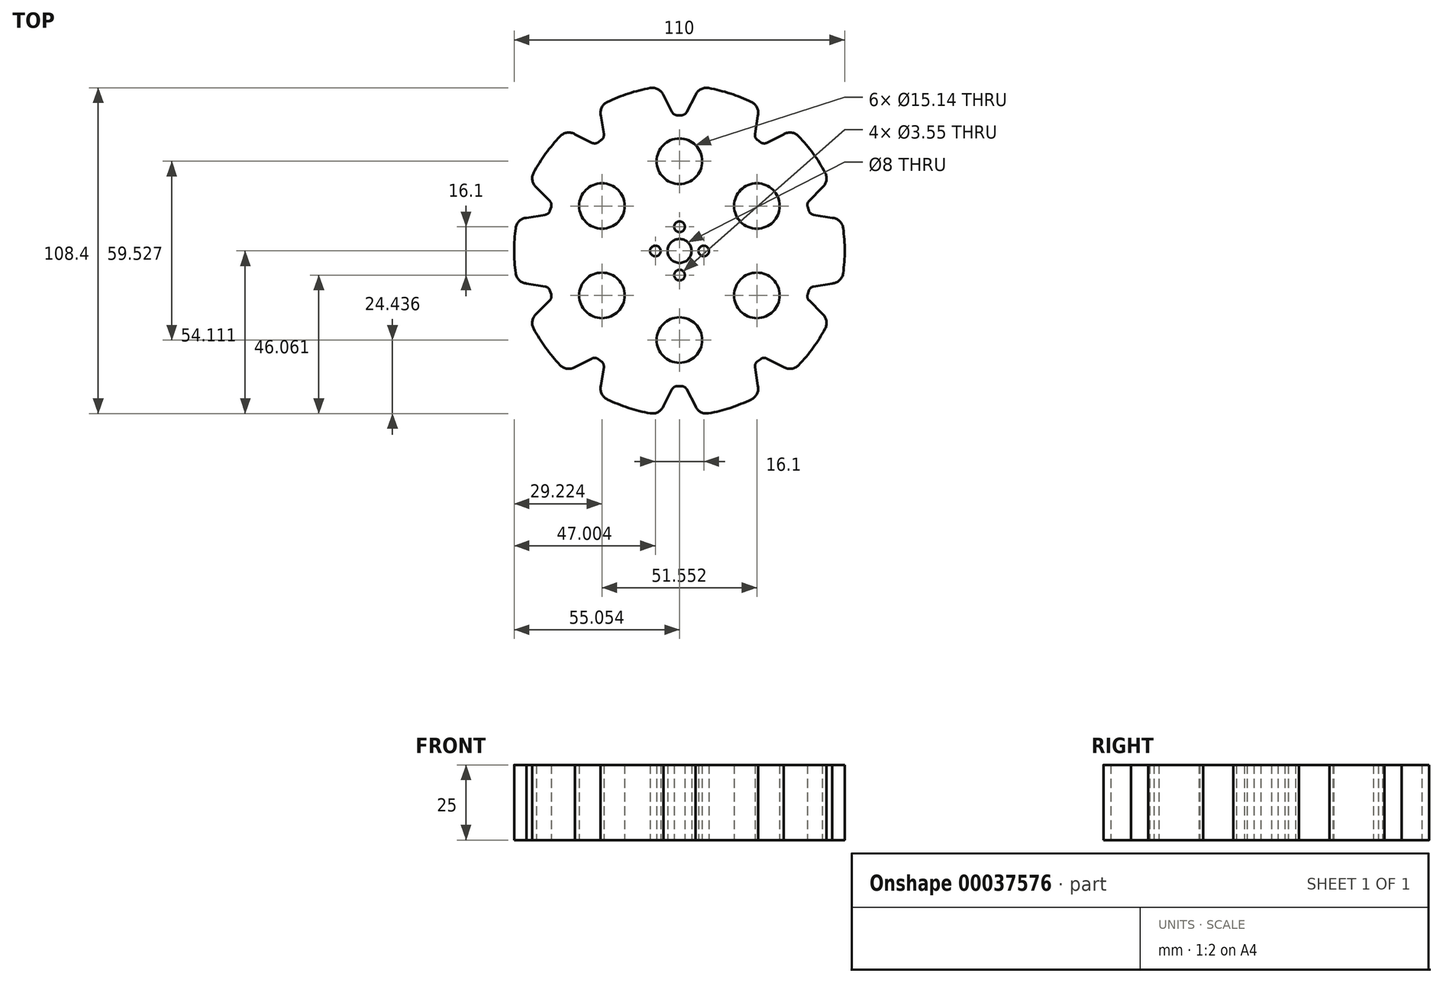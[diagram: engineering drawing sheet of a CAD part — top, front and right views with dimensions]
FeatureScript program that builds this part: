
annotation { "Feature Type Name" : "Feature", "Feature Type Description" : "" }
export const myFeature = defineFeature(function(context is Context, id is Id, definition is map)
    precondition{}
    {
        {
            var Q0;
            Q0=qCreatedBy(makeId("Top.planeOp"),FACE);
            var sketch = newSketch(context, id + "F0", { "sketchPlane" : qUnion([Q0])});
            skArc(sketch, "E0", {"start": v(-9.7, 54.14) * mm, "mid": v(-17, 52.3) * mm, "end": v(-23.97, 49.5) * mm});
            skPoint(sketch, "E1.visualSharp", {"position": v(5, 54.77) * mm});
            skArc(sketch, "E1.filletArc", {"start": v(9.7, 54.14) * mm, "mid": v(7.09, 53.71) * mm, "end": v(5.3, 51.74) * mm});
            skPoint(sketch, "E2.visualSharp", {"position": v(-5, 54.77) * mm});
            skArc(sketch, "E2.filletArc", {"start": v(-5.3, 51.74) * mm, "mid": v(-7.09, 53.71) * mm, "end": v(-9.7, 54.14) * mm});
            skLineSegment(sketch, "E3", {"start": v(-5.3, 51.74) * mm, "end": v(-2.44, 46.17) * mm});
            skArc(sketch, "E4.filletArc", {"start": v(-2.44, 46.17) * mm, "mid": v(-1.7, 45.38) * mm, "end": v(-0.67, 45.09) * mm});
            skArc(sketch, "E5.MirrorCS", {"start": v(2.44, 46.17) * mm, "mid": v(1.7, 45.38) * mm, "end": v(0.67, 45.09) * mm});
            skLineSegment(sketch, "E6.MirrorCS", {"start": v(5.3, 51.74) * mm, "end": v(2.44, 46.17) * mm});
            skLineSegment(sketch, "E7", {"start": v(-0.67, 45.09) * mm, "end": v(0.67, 45.09) * mm});
            skArc(sketch, "E8.1.0", {"start": v(-34.7, 38.74) * mm, "mid": v(-37.3, 39.29) * mm, "end": v(-39.67, 38.1) * mm});
            skLineSegment(sketch, "E8.1.1", {"start": v(-26.12, 44.98) * mm, "end": v(-25.16, 38.79) * mm});
            skPoint(sketch, "E8.1.2", {"position": v(-28.15, 47.25) * mm});
            skArc(sketch, "E8.1.3", {"start": v(-23.97, 49.5) * mm, "mid": v(-25.84, 47.62) * mm, "end": v(-26.12, 44.98) * mm});
            skLineSegment(sketch, "E8.1.4", {"start": v(-34.7, 38.74) * mm, "end": v(-29.12, 35.92) * mm});
            skPoint(sketch, "E8.1.5", {"position": v(-36.24, 41.37) * mm});
            skLineSegment(sketch, "E8.1.6", {"start": v(-27.04, 36.08) * mm, "end": v(-25.96, 36.87) * mm});
            skArc(sketch, "E8.1.7", {"start": v(-29.12, 35.92) * mm, "mid": v(-28.05, 35.7) * mm, "end": v(-27.04, 36.08) * mm});
            skArc(sketch, "E8.1.8", {"start": v(-25.16, 38.79) * mm, "mid": v(-25.3, 37.71) * mm, "end": v(-25.96, 36.87) * mm});
            skArc(sketch, "E8.2.0", {"start": v(-50.85, 10.94) * mm, "mid": v(-53.27, 9.86) * mm, "end": v(-54.49, 7.5) * mm});
            skLineSegment(sketch, "E8.2.1", {"start": v(-47.57, 21.04) * mm, "end": v(-43.16, 16.6) * mm});
            skPoint(sketch, "E8.2.2", {"position": v(-50.55, 21.68) * mm});
            skArc(sketch, "E8.2.3", {"start": v(-48.49, 25.96) * mm, "mid": v(-48.9, 23.34) * mm, "end": v(-47.57, 21.04) * mm});
            skLineSegment(sketch, "E8.2.4", {"start": v(-50.85, 10.94) * mm, "end": v(-44.67, 11.94) * mm});
            skPoint(sketch, "E8.2.5", {"position": v(-53.64, 12.17) * mm});
            skLineSegment(sketch, "E8.2.6", {"start": v(-43.08, 13.3) * mm, "end": v(-42.67, 14.56) * mm});
            skArc(sketch, "E8.2.7", {"start": v(-44.67, 11.94) * mm, "mid": v(-43.68, 12.4) * mm, "end": v(-43.08, 13.3) * mm});
            skArc(sketch, "E8.2.8", {"start": v(-43.16, 16.6) * mm, "mid": v(-42.63, 15.65) * mm, "end": v(-42.67, 14.56) * mm});
            skArc(sketch, "E8.3.0", {"start": v(-47.57, -21.04) * mm, "mid": v(-48.9, -23.34) * mm, "end": v(-48.49, -25.96) * mm});
            skLineSegment(sketch, "E8.3.1", {"start": v(-50.85, -10.94) * mm, "end": v(-44.67, -11.94) * mm});
            skPoint(sketch, "E8.3.2", {"position": v(-53.64, -12.17) * mm});
            skArc(sketch, "E8.3.3", {"start": v(-54.49, -7.5) * mm, "mid": v(-53.27, -9.86) * mm, "end": v(-50.85, -10.94) * mm});
            skLineSegment(sketch, "E8.3.4", {"start": v(-47.57, -21.04) * mm, "end": v(-43.16, -16.6) * mm});
            skPoint(sketch, "E8.3.5", {"position": v(-50.55, -21.68) * mm});
            skLineSegment(sketch, "E8.3.6", {"start": v(-42.67, -14.56) * mm, "end": v(-43.08, -13.3) * mm});
            skArc(sketch, "E8.3.7", {"start": v(-43.16, -16.6) * mm, "mid": v(-42.63, -15.65) * mm, "end": v(-42.67, -14.56) * mm});
            skArc(sketch, "E8.3.8", {"start": v(-44.67, -11.94) * mm, "mid": v(-43.68, -12.4) * mm, "end": v(-43.08, -13.3) * mm});
            skArc(sketch, "E8.4.0", {"start": v(-26.12, -44.98) * mm, "mid": v(-25.84, -47.62) * mm, "end": v(-23.97, -49.5) * mm});
            skLineSegment(sketch, "E8.4.1", {"start": v(-34.7, -38.74) * mm, "end": v(-29.12, -35.92) * mm});
            skPoint(sketch, "E8.4.2", {"position": v(-36.24, -41.37) * mm});
            skArc(sketch, "E8.4.3", {"start": v(-39.67, -38.1) * mm, "mid": v(-37.3, -39.29) * mm, "end": v(-34.7, -38.74) * mm});
            skLineSegment(sketch, "E8.4.4", {"start": v(-26.12, -44.98) * mm, "end": v(-25.16, -38.79) * mm});
            skPoint(sketch, "E8.4.5", {"position": v(-28.15, -47.25) * mm});
            skLineSegment(sketch, "E8.4.6", {"start": v(-25.96, -36.87) * mm, "end": v(-27.04, -36.08) * mm});
            skArc(sketch, "E8.4.7", {"start": v(-25.16, -38.79) * mm, "mid": v(-25.3, -37.71) * mm, "end": v(-25.96, -36.87) * mm});
            skArc(sketch, "E8.4.8", {"start": v(-29.12, -35.92) * mm, "mid": v(-28.05, -35.7) * mm, "end": v(-27.04, -36.08) * mm});
            skArc(sketch, "E8.5.0", {"start": v(5.3, -51.74) * mm, "mid": v(7.09, -53.71) * mm, "end": v(9.7, -54.14) * mm});
            skLineSegment(sketch, "E8.5.1", {"start": v(-5.3, -51.74) * mm, "end": v(-2.44, -46.17) * mm});
            skPoint(sketch, "E8.5.2", {"position": v(-5, -54.77) * mm});
            skArc(sketch, "E8.5.3", {"start": v(-9.7, -54.14) * mm, "mid": v(-7.09, -53.71) * mm, "end": v(-5.3, -51.74) * mm});
            skLineSegment(sketch, "E8.5.4", {"start": v(5.3, -51.74) * mm, "end": v(2.44, -46.17) * mm});
            skPoint(sketch, "E8.5.5", {"position": v(5, -54.77) * mm});
            skLineSegment(sketch, "E8.5.6", {"start": v(0.67, -45.09) * mm, "end": v(-0.67, -45.09) * mm});
            skArc(sketch, "E8.5.7", {"start": v(2.44, -46.17) * mm, "mid": v(1.7, -45.38) * mm, "end": v(0.67, -45.09) * mm});
            skArc(sketch, "E8.5.8", {"start": v(-2.44, -46.17) * mm, "mid": v(-1.7, -45.38) * mm, "end": v(-0.67, -45.09) * mm});
            skArc(sketch, "E8.6.0", {"start": v(34.7, -38.74) * mm, "mid": v(37.3, -39.29) * mm, "end": v(39.67, -38.1) * mm});
            skLineSegment(sketch, "E8.6.1", {"start": v(26.12, -44.98) * mm, "end": v(25.16, -38.79) * mm});
            skPoint(sketch, "E8.6.2", {"position": v(28.15, -47.25) * mm});
            skArc(sketch, "E8.6.3", {"start": v(23.97, -49.5) * mm, "mid": v(25.84, -47.62) * mm, "end": v(26.12, -44.98) * mm});
            skLineSegment(sketch, "E8.6.4", {"start": v(34.7, -38.74) * mm, "end": v(29.12, -35.92) * mm});
            skPoint(sketch, "E8.6.5", {"position": v(36.24, -41.37) * mm});
            skLineSegment(sketch, "E8.6.6", {"start": v(27.04, -36.08) * mm, "end": v(25.96, -36.87) * mm});
            skArc(sketch, "E8.6.7", {"start": v(29.12, -35.92) * mm, "mid": v(28.05, -35.7) * mm, "end": v(27.04, -36.08) * mm});
            skArc(sketch, "E8.6.8", {"start": v(25.16, -38.79) * mm, "mid": v(25.3, -37.71) * mm, "end": v(25.96, -36.87) * mm});
            skArc(sketch, "E8.7.0", {"start": v(50.85, -10.94) * mm, "mid": v(53.27, -9.86) * mm, "end": v(54.49, -7.5) * mm});
            skLineSegment(sketch, "E8.7.1", {"start": v(47.57, -21.04) * mm, "end": v(43.16, -16.6) * mm});
            skPoint(sketch, "E8.7.2", {"position": v(50.55, -21.68) * mm});
            skArc(sketch, "E8.7.3", {"start": v(48.49, -25.96) * mm, "mid": v(48.9, -23.34) * mm, "end": v(47.57, -21.04) * mm});
            skLineSegment(sketch, "E8.7.4", {"start": v(50.85, -10.94) * mm, "end": v(44.67, -11.94) * mm});
            skPoint(sketch, "E8.7.5", {"position": v(53.64, -12.17) * mm});
            skLineSegment(sketch, "E8.7.6", {"start": v(43.08, -13.3) * mm, "end": v(42.67, -14.56) * mm});
            skArc(sketch, "E8.7.7", {"start": v(44.67, -11.94) * mm, "mid": v(43.68, -12.4) * mm, "end": v(43.08, -13.3) * mm});
            skArc(sketch, "E8.7.8", {"start": v(43.16, -16.6) * mm, "mid": v(42.63, -15.65) * mm, "end": v(42.67, -14.56) * mm});
            skArc(sketch, "E8.8.0", {"start": v(47.57, 21.04) * mm, "mid": v(48.9, 23.34) * mm, "end": v(48.49, 25.96) * mm});
            skLineSegment(sketch, "E8.8.1", {"start": v(50.85, 10.94) * mm, "end": v(44.67, 11.94) * mm});
            skPoint(sketch, "E8.8.2", {"position": v(53.64, 12.17) * mm});
            skArc(sketch, "E8.8.3", {"start": v(54.49, 7.5) * mm, "mid": v(53.27, 9.86) * mm, "end": v(50.85, 10.94) * mm});
            skLineSegment(sketch, "E8.8.4", {"start": v(47.57, 21.04) * mm, "end": v(43.16, 16.6) * mm});
            skPoint(sketch, "E8.8.5", {"position": v(50.55, 21.68) * mm});
            skLineSegment(sketch, "E8.8.6", {"start": v(42.67, 14.56) * mm, "end": v(43.08, 13.3) * mm});
            skArc(sketch, "E8.8.7", {"start": v(43.16, 16.6) * mm, "mid": v(42.63, 15.65) * mm, "end": v(42.67, 14.56) * mm});
            skArc(sketch, "E8.8.8", {"start": v(44.67, 11.94) * mm, "mid": v(43.68, 12.4) * mm, "end": v(43.08, 13.3) * mm});
            skArc(sketch, "E8.9.0", {"start": v(26.12, 44.98) * mm, "mid": v(25.84, 47.62) * mm, "end": v(23.97, 49.5) * mm});
            skLineSegment(sketch, "E8.9.1", {"start": v(34.7, 38.74) * mm, "end": v(29.12, 35.92) * mm});
            skPoint(sketch, "E8.9.2", {"position": v(36.24, 41.37) * mm});
            skArc(sketch, "E8.9.3", {"start": v(39.67, 38.1) * mm, "mid": v(37.3, 39.29) * mm, "end": v(34.7, 38.74) * mm});
            skLineSegment(sketch, "E8.9.4", {"start": v(26.12, 44.98) * mm, "end": v(25.16, 38.79) * mm});
            skPoint(sketch, "E8.9.5", {"position": v(28.15, 47.25) * mm});
            skLineSegment(sketch, "E8.9.6", {"start": v(25.96, 36.87) * mm, "end": v(27.04, 36.08) * mm});
            skArc(sketch, "E8.9.7", {"start": v(25.16, 38.79) * mm, "mid": v(25.3, 37.71) * mm, "end": v(25.96, 36.87) * mm});
            skArc(sketch, "E8.9.8", {"start": v(29.12, 35.92) * mm, "mid": v(28.05, 35.7) * mm, "end": v(27.04, 36.08) * mm});
            skArc(sketch, "E9.trimOffspring", {"start": v(-39.67, 38.1) * mm, "mid": v(-44.5, 32.33) * mm, "end": v(-48.49, 25.96) * mm});
            skArc(sketch, "E10.trimOffspring", {"start": v(-54.49, 7.5) * mm, "mid": v(-55, 0) * mm, "end": v(-54.49, -7.5) * mm});
            skArc(sketch, "E11.trimOffspring", {"start": v(23.97, 49.5) * mm, "mid": v(17, 52.3) * mm, "end": v(9.7, 54.14) * mm});
            skArc(sketch, "E12.trimOffspring", {"start": v(48.49, 25.96) * mm, "mid": v(44.5, 32.33) * mm, "end": v(39.67, 38.1) * mm});
            skArc(sketch, "E13.trimOffspring", {"start": v(-48.49, -25.96) * mm, "mid": v(-44.5, -32.33) * mm, "end": v(-39.67, -38.1) * mm});
            skArc(sketch, "E14.trimOffspring", {"start": v(-23.97, -49.5) * mm, "mid": v(-17, -52.3) * mm, "end": v(-9.7, -54.14) * mm});
            skArc(sketch, "E15.trimOffspring", {"start": v(9.7, -54.14) * mm, "mid": v(17, -52.3) * mm, "end": v(23.97, -49.5) * mm});
            skArc(sketch, "E16.trimOffspring", {"start": v(39.67, -38.1) * mm, "mid": v(44.5, -32.33) * mm, "end": v(48.49, -25.96) * mm});
            skArc(sketch, "E17.trimOffspring", {"start": v(54.49, -7.5) * mm, "mid": v(55, 0) * mm, "end": v(54.49, 7.5) * mm});
            skLineSegment(sketch, "E18", {"start": v(-55, 0) * mm, "end": v(55, 0) * mm, "construction": true});
            skCircle(sketch, "E19", {"center": v(0.05, -0.09) * mm, "radius": 4 * mm});
            skCircle(sketch, "E20", {"center": v(0.05, 7.96) * mm, "radius": 1.77 * mm});
            skCircle(sketch, "E21.2.0", {"center": v(0.05, -8.14) * mm, "radius": 1.77 * mm});
            skCircle(sketch, "E21.1.0", {"center": v(-8, -0.09) * mm, "radius": 1.77 * mm});
            skCircle(sketch, "E21.3.0", {"center": v(8.1, -0.09) * mm, "radius": 1.77 * mm});
            skCircle(sketch, "E22", {"center": v(0, 29.76) * mm, "radius": 7.57 * mm});
            skCircle(sketch, "E23.1.0", {"center": v(-25.78, 14.88) * mm, "radius": 7.57 * mm});
            skCircle(sketch, "E23.2.0", {"center": v(-25.78, -14.88) * mm, "radius": 7.57 * mm});
            skCircle(sketch, "E23.3.0", {"center": v(0, -29.76) * mm, "radius": 7.57 * mm});
            skCircle(sketch, "E23.4.0", {"center": v(25.78, -14.88) * mm, "radius": 7.57 * mm});
            skCircle(sketch, "E23.5.0", {"center": v(25.78, 14.88) * mm, "radius": 7.57 * mm});
            skSolve(sketch);
        }
        {
            var Q0;
            Q0=makeQuery(id+"F0.imprint","IMPRINT",FACE,{"disambiguationData":[TD([[makeQuery(id+"F0.imprint","IMPRINT",EDGE,{"derivedFrom":sQuery(id+"F0.wireOp",EDGE,"E0")}),1.0]])]});
            extrude(context, id + "F1", {"entities" : qUnion([Q0]), "depth" : 25 * mm});
        }
    });
